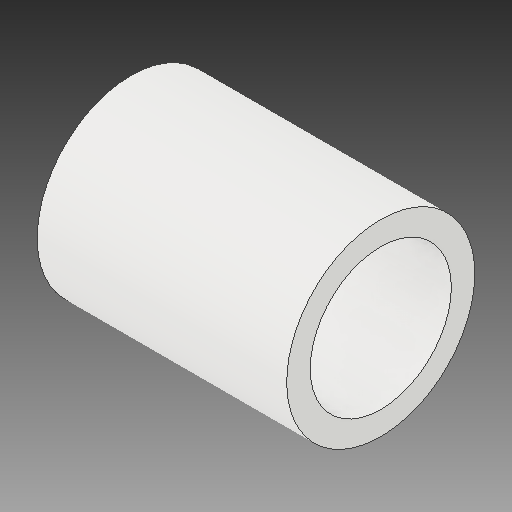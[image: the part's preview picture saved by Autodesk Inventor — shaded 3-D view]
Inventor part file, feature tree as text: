
AUTODESK INVENTOR PART (.ipt)
format: ipt  version: 2019 (Build 230136000, 136)  size: 111,104 bytes
history: native  units: mm
features: extrude x1, sketch x1
ambient origin geometry x8: Origin, YZ Plane, XZ Plane, XY Plane, X Axis, Y Axis, Z Axis, Center Point
bodies: Body1 (feature_tree)
feature tree (2):
  extrude  "Extrusion1"  Depth=21.228mm
  sketch  "Sketch1"  dims[d1=16.0mm d2=12.0mm d3=21.228mm d4=0.0mm]
